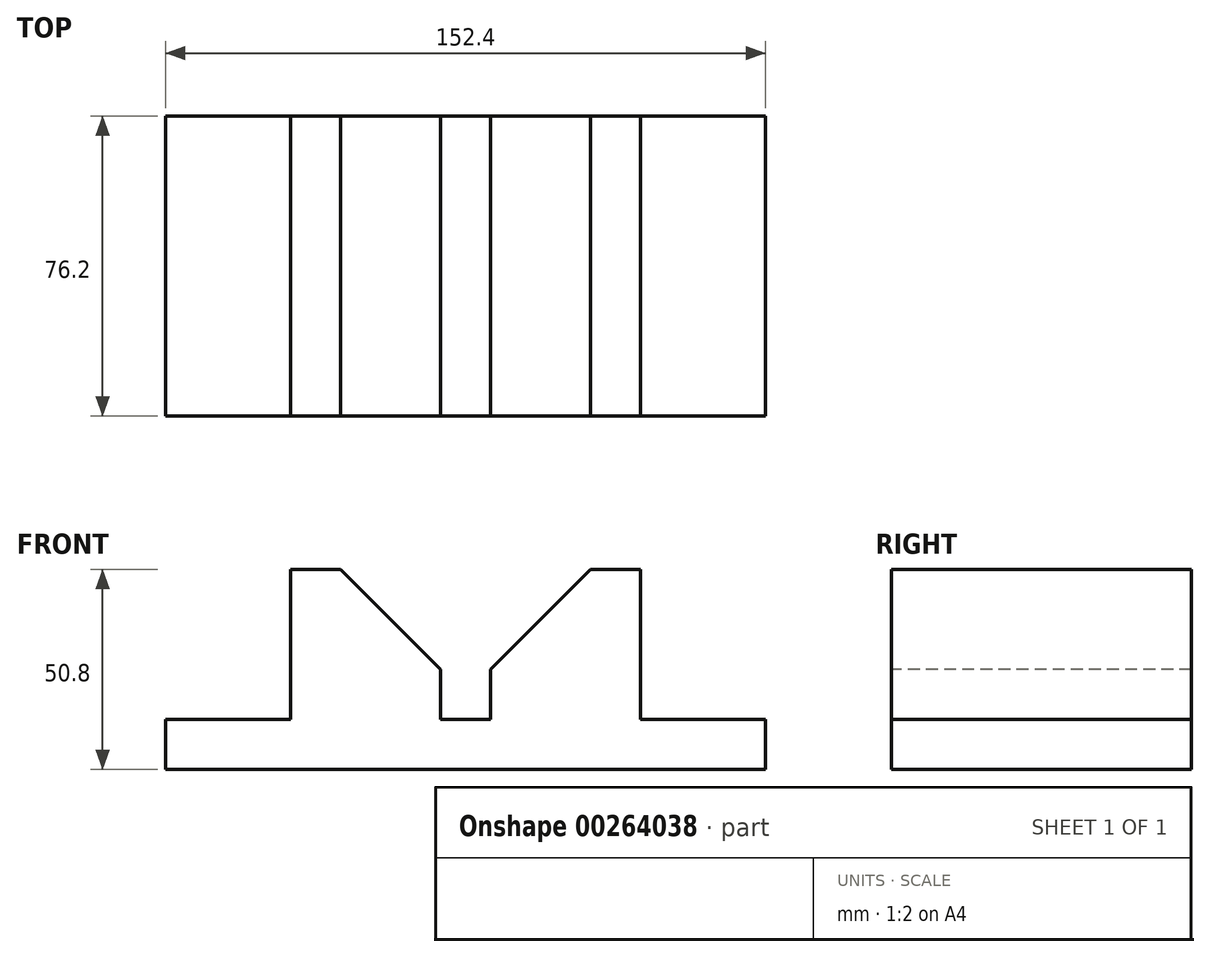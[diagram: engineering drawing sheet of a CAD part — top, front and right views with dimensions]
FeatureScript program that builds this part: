
annotation { "Feature Type Name" : "Feature", "Feature Type Description" : "" }
export const myFeature = defineFeature(function(context is Context, id is Id, definition is map)
    precondition{}
    {
        {
            var Q0;
            Q0=qCreatedBy(makeId("Front.planeOp"),FACE);
            var sketch = newSketch(context, id + "F0", { "sketchPlane" : qUnion([Q0])});
            skLineSegment(sketch, "E0", {"start": v(-63.09, -12.7) * mm, "end": v(89.31, -12.7) * mm});
            skLineSegment(sketch, "E1", {"start": v(89.31, -12.7) * mm, "end": v(89.31, 0) * mm});
            skLineSegment(sketch, "E2", {"start": v(89.31, 0) * mm, "end": v(57.56, 0) * mm});
            skLineSegment(sketch, "E3", {"start": v(57.56, 0) * mm, "end": v(57.56, 38.1) * mm});
            skLineSegment(sketch, "E4", {"start": v(57.56, 38.1) * mm, "end": v(44.86, 38.1) * mm});
            skLineSegment(sketch, "E5", {"start": v(44.86, 38.1) * mm, "end": v(-18.64, 38.1) * mm});
            skLineSegment(sketch, "E6", {"start": v(-18.64, 38.1) * mm, "end": v(-31.34, 38.1) * mm});
            skLineSegment(sketch, "E7", {"start": v(-31.34, 38.1) * mm, "end": v(-31.34, 0) * mm});
            skLineSegment(sketch, "E8", {"start": v(-31.34, 0) * mm, "end": v(-63.09, 0) * mm});
            skLineSegment(sketch, "E9", {"start": v(-63.09, 0) * mm, "end": v(-63.09, -12.7) * mm});
            skLineSegment(sketch, "E10", {"start": v(-31.34, 38.1) * mm, "end": v(-31.34, 19.05) * mm});
            skSolve(sketch);
        }
        {
            var Q0;
            Q0=makeQuery(id+"F0.imprint","IMPRINT",FACE,{"disambiguationData":[TD([[makeQuery(id+"F0.imprint","IMPRINT",EDGE,{"derivedFrom":sQuery(id+"F0.wireOp",EDGE,"E0")}),1.0]])]});
            extrude(context, id + "F1", {"entities" : qUnion([Q0]), "depth" : 38.1 * mm});
        }
        {
            var Q0;
            Q0=makeQuery(id+"F1.opExtrude","CAP_FACE",FACE,{"disambiguationData":[OSD([sQuery(id+"F0.wireOp",EDGE,"E0"),sQuery(id+"F0.wireOp",EDGE,"E1"),sQuery(id+"F0.wireOp",EDGE,"E2"),sQuery(id+"F0.wireOp",EDGE,"E3"),sQuery(id+"F0.wireOp",EDGE,"E4"),sQuery(id+"F0.wireOp",EDGE,"E5"),sQuery(id+"F0.wireOp",EDGE,"E6"),sQuery(id+"F0.wireOp",EDGE,"E7"),sQuery(id+"F0.wireOp",EDGE,"E8"),sQuery(id+"F0.wireOp",EDGE,"E9"),sQuery(id+"F0.wireOp",EDGE,"E10")])],"isStart":true});
            var Q1;
            Q1=makeQuery(id+"F1.opExtrude","CAP_FACE",FACE,{"disambiguationData":[OSD([sQuery(id+"F0.wireOp",EDGE,"E0"),sQuery(id+"F0.wireOp",EDGE,"E1"),sQuery(id+"F0.wireOp",EDGE,"E2"),sQuery(id+"F0.wireOp",EDGE,"E3"),sQuery(id+"F0.wireOp",EDGE,"E4"),sQuery(id+"F0.wireOp",EDGE,"E5"),sQuery(id+"F0.wireOp",EDGE,"E6"),sQuery(id+"F0.wireOp",EDGE,"E7"),sQuery(id+"F0.wireOp",EDGE,"E8"),sQuery(id+"F0.wireOp",EDGE,"E9"),sQuery(id+"F0.wireOp",EDGE,"E10")])],"isStart":false});
            extrude(context, id + "F2", {"entities" : qUnion([Q0, Q1]), "operationType" : NewBodyOperationType.ADD, "depth" : 38.1 * mm});
        }
        {
            var Q0;
            Q0=makeQuery(id+"F1.opExtrude","CAP_FACE",FACE,{"disambiguationData":[OSD([sQuery(id+"F0.wireOp",EDGE,"E0"),sQuery(id+"F0.wireOp",EDGE,"E1"),sQuery(id+"F0.wireOp",EDGE,"E2"),sQuery(id+"F0.wireOp",EDGE,"E3"),sQuery(id+"F0.wireOp",EDGE,"E4"),sQuery(id+"F0.wireOp",EDGE,"E5"),sQuery(id+"F0.wireOp",EDGE,"E6"),sQuery(id+"F0.wireOp",EDGE,"E7"),sQuery(id+"F0.wireOp",EDGE,"E8"),sQuery(id+"F0.wireOp",EDGE,"E9"),sQuery(id+"F0.wireOp",EDGE,"E10")])],"isStart":false});
            var sketch = newSketch(context, id + "F3", { "sketchPlane" : qUnion([Q0])});
            skLineSegment(sketch, "E11", {"start": v(-31.34, 38.1) * mm, "end": v(-31.34, 12.7) * mm});
            skLineSegment(sketch, "E12", {"start": v(-31.34, 12.7) * mm, "end": v(6.76, 12.7) * mm});
            skLineSegment(sketch, "E13", {"start": v(6.76, 12.7) * mm, "end": v(19.46, 12.7) * mm});
            skLineSegment(sketch, "E14", {"start": v(19.46, 12.7) * mm, "end": v(57.56, 12.7) * mm});
            skLineSegment(sketch, "E15", {"start": v(57.56, 12.7) * mm, "end": v(57.56, 38.1) * mm});
            skLineSegment(sketch, "E16", {"start": v(57.56, 38.1) * mm, "end": v(44.86, 38.1) * mm});
            skLineSegment(sketch, "E17", {"start": v(44.86, 38.1) * mm, "end": v(19.46, 12.7) * mm});
            skLineSegment(sketch, "E18", {"start": v(6.76, 12.7) * mm, "end": v(-31.34, 12.7) * mm});
            skLineSegment(sketch, "E19", {"start": v(-31.34, 38.1) * mm, "end": v(-18.64, 38.1) * mm});
            skLineSegment(sketch, "E20", {"start": v(-18.64, 38.1) * mm, "end": v(6.76, 12.7) * mm});
            skLineSegment(sketch, "E21", {"start": v(6.76, 0) * mm, "end": v(19.46, 0) * mm});
            skLineSegment(sketch, "E22", {"start": v(19.46, 0) * mm, "end": v(19.46, 12.7) * mm});
            skLineSegment(sketch, "E23", {"start": v(6.76, 12.7) * mm, "end": v(6.76, 0) * mm});
            skSolve(sketch);
        }
        {
            var Q0;
            Q0=makeQuery(id+"F3.imprint","IMPRINT",FACE,{"disambiguationData":[TD([[makeQuery(id+"F3.imprint","IMPRINT",EDGE,{"derivedFrom":sQuery(id+"F3.wireOp",EDGE,"E13")}),1.0]])]});
            var Q1;
            Q1=makeQuery(id+"F3.imprint","IMPRINT",FACE,{"disambiguationData":[TD([[makeQuery(id+"F3.imprint","IMPRINT",EDGE,{"derivedFrom":sQuery(id+"F3.wireOp",EDGE,"E13")}),-1.0]])]});
            extrude(context, id + "F4", {"entities" : qUnion([Q0, Q1]), "operationType" : NewBodyOperationType.REMOVE, "oppositeDirection" : true, "depth" : 76.2 * mm});
        }
    });
